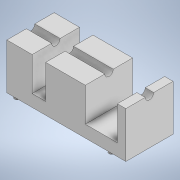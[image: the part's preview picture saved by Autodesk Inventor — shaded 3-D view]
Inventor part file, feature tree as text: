
AUTODESK INVENTOR PART (.ipt)
format: ipt  version: 2021 (Build 250183000, 183)  size: 141,824 bytes
history: native  units: mm
features: extrude x4, sketch x4
ambient origin geometry x8: Origin, YZ Plane, XZ Plane, XY Plane, X Axis, Y Axis, Z Axis, Center Point
bodies: Body1 (feature_tree)
feature tree (8):
  extrude  "Extrusion3"  Depth=28.024mm
  extrude  "Extrusion4"  Depth=27.147mm TaperAngle=0.0deg
  extrude  "Extrusion5"  Depth=15.0mm
  extrude  "Extrusion6"  Depth=46.5mm
  sketch  "Sketch7"  dims[d32=70.5mm d34=28.024mm]
  sketch  "Sketch8"  dims[d35=14.012mm d37=27.147mm d38=0.0mm]
  sketch  "Sketch9"  dims[d39=20.0mm d40=15.0mm]
  sketch  "Sketch10"  dims[d41=8.0mm d42=46.5mm d44=5.0mm d45=0.0mm d46=0.0mm d47=5.0mm d48=0.0mm d49=0.0mm d50=3.0mm d51=2.5mm d52=3.0mm d54=3.0mm d55=0.0mm d56=56.0mm d57=3.5mm d58=3.5mm]
